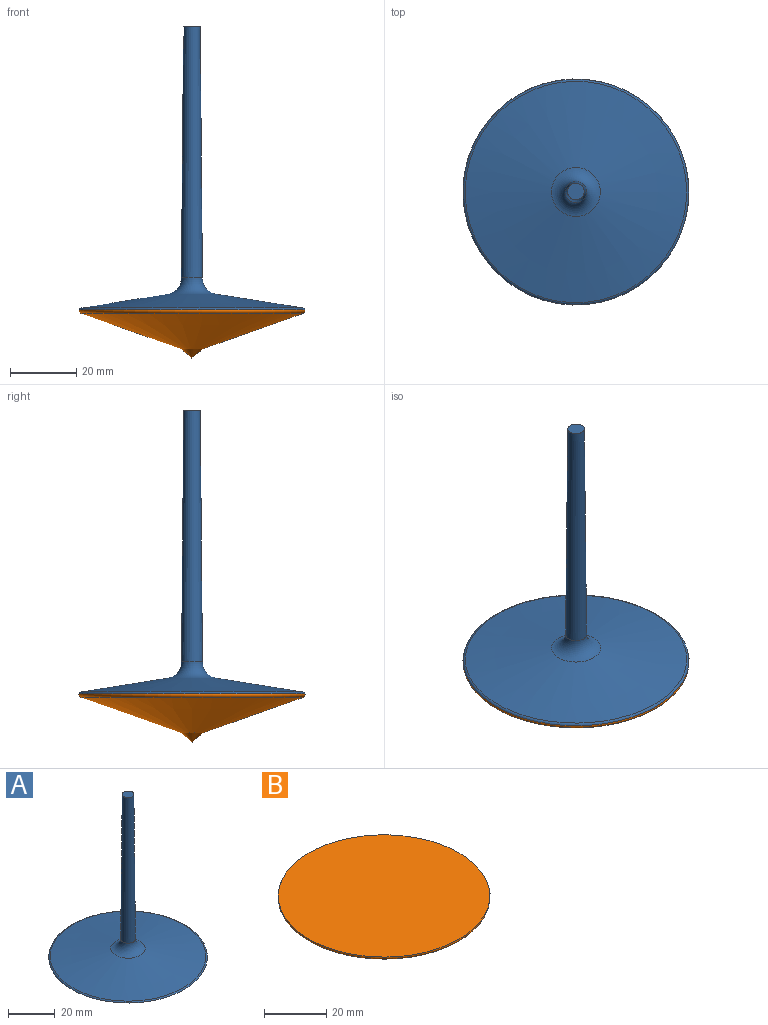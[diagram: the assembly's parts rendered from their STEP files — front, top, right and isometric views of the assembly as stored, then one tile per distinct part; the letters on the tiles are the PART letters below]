
ASSEMBLY  parts=2 mates=1
PART A: 6 faces, bbox 73.7x73.7x85.8 mm
  f0: cone r=7.37mm half-angle=80.9deg, axis (0,0,-1), area 3365.6mm2, adj f1,f5
  f1: torus R=33.22mm, axis (0,0,1), area 184.4mm2, adj f0,f2
  f2: plane 68x68mm, normal (0,0,-1), area 3631.5mm2, adj f1
  f3: plane 5x5mm, normal (0,0,1), area 19.6mm2, adj f4
  f4: cone r=2.5mm half-angle=0.5deg, axis (0,0,-1), area 1349.9mm2, adj f3,f5
  f5: torus R=8.16mm, axis (0,0,1), area 206.2mm2, adj f0,f4
PART B: 4 faces, bbox 73.7x73.7x14.8 mm
  f0: plane 68x68mm, normal (0,0,1), area 3631.5mm2, adj f1
  f1: torus R=33.22mm, axis (0,0,1), area 287.8mm2, adj f0,f2
  f2: cone r=33.5mm half-angle=70.5deg, axis (0,0,1), area 3703.6mm2, adj f1,f3
  f3: cone r=3.28mm half-angle=50deg, axis (0,0,1), area 44.2mm2, adj f2
PLACE A t=(-36.08,0.51,26.04)mm fixed
PLACE B t=(-36.08,-15.48,-7.72)mm
MATE fastened B.f1 <-> A.f0  axis (0,0,1) through (-36.08,0.51,-10.71)mm
